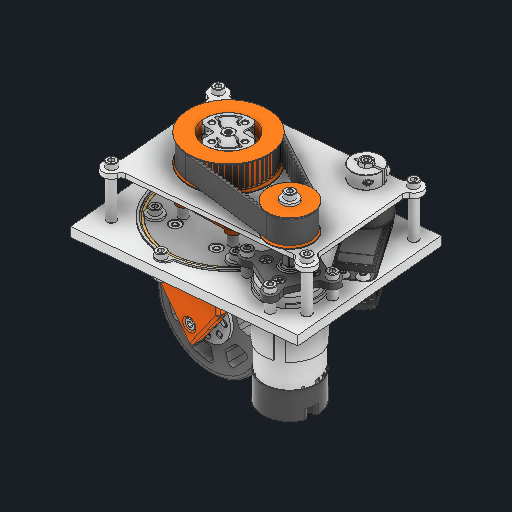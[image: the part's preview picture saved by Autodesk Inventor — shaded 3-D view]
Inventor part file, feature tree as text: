
AUTODESK INVENTOR PART (.ipt)
format: ipt  version: 2024.2 (Build 282272000, 272)  size: 62,758,400 bytes
history: native  units: in
note: dims shown in document units (in); Inventor stores cm internally (conversion verified against a paired STEP export)
features: other x3, plane x1
ambient origin geometry x8: Origin, YZ Plane, XZ Plane, XY Plane, X Axis, Y Axis, Z Axis, Center Point
bodies: Solid1 (feature_tree)
feature tree (4):
  other  "Pod_pre_mirror.ipt"
  other  "Solid1::Pod_pre_mirror.ipt"
  other  "TaggingFeature1"
  plane  "Work Plane2_1"
